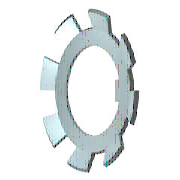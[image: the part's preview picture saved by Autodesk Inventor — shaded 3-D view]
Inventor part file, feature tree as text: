
AUTODESK INVENTOR PART (.ipt)
format: ipt  version: 2022 (Build 260153000, 153)  size: 211,456 bytes
history: native  units: mm (DEFAULTED — no unit token found)
features: sketch x2, extrude x2, pattern_circular x1, other x1, plane x1
ambient origin geometry x8: Origin, YZ Plane, XZ Plane, XY Plane, X Axis, Y Axis, Z Axis, Center Point
bodies: Solid1 (feature_tree), Body (feature_tree)
feature tree (7):
  sketch  "Sketch2"  dims[d3=61.0mm d4=74.0mm d5=4.363323mm d6=1.25mm d7=90.0deg d8=50.0mm d9=6.0mm d10=22.5mm d16=1.208305mm d17=1.25mm d18=0.0mm d19=1.25mm d20=0.0mm d21=130.0mm d23=360.0deg d24=0.0mm d25=0.0mm d26=90.0deg d27=0.0mm]
  extrude  "Cut"  Depth=1.25mm
  extrude  "Nib"  Depth=1.25mm
  pattern_circular  "Cuts"  [2 undecoded]
  other  "Work Axis1"
  plane  "Work Plane1"
  sketch  "Sketch1"  dims[d1=1.25mm d2=50.0mm]
note: 2 required parameter values undecoded (feature->parameter linkage not recoverable at this tier; creation-order binding heuristic only, values carry confidence <= 0.55)
